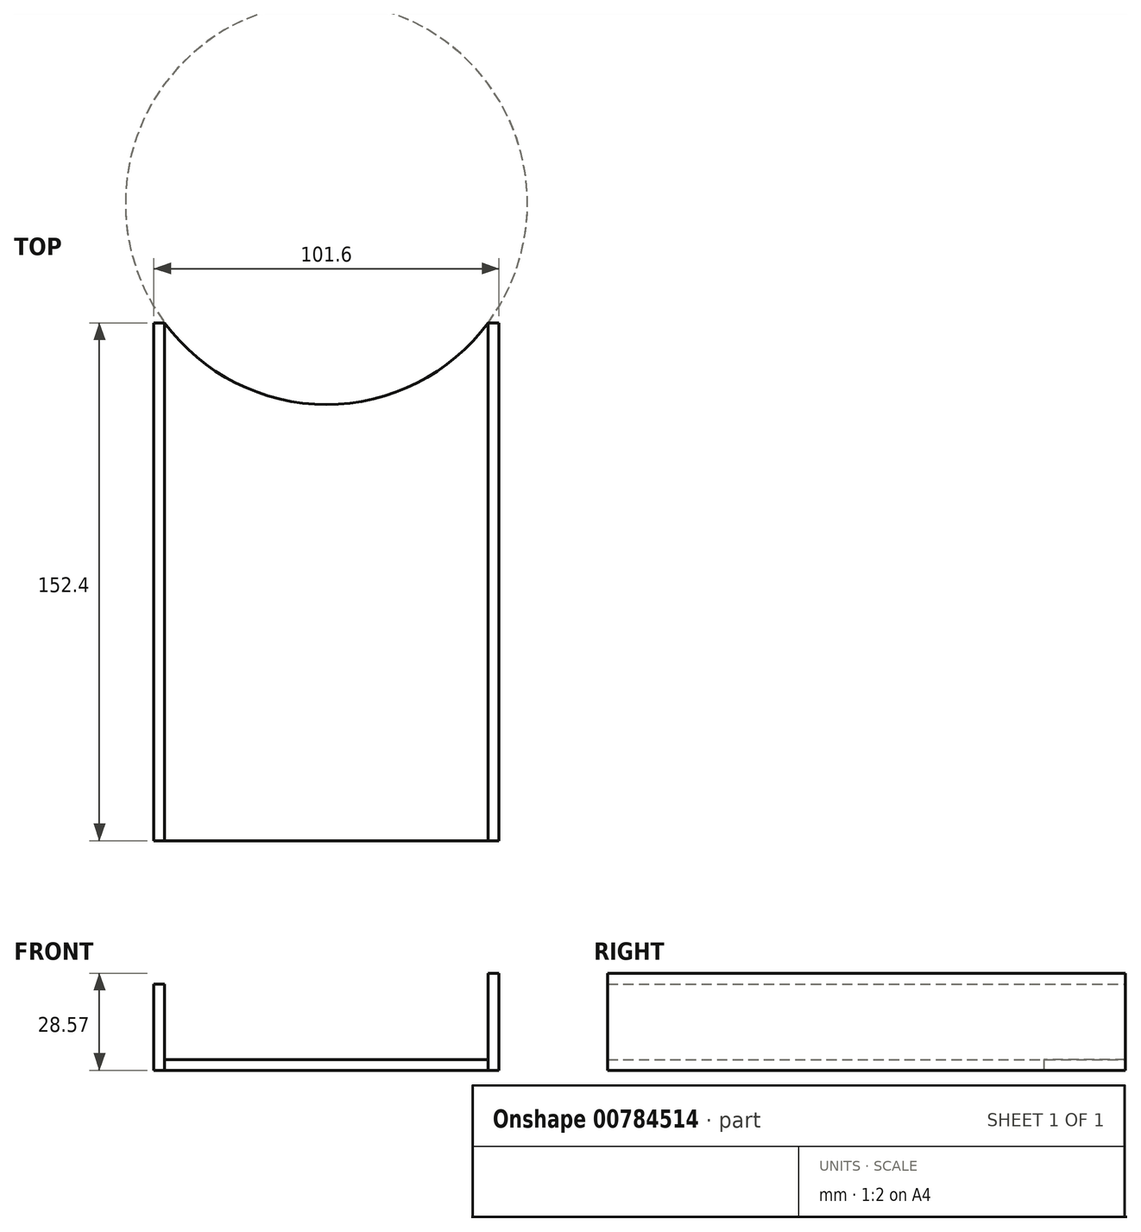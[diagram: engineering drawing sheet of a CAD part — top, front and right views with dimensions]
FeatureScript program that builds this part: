
annotation { "Feature Type Name" : "Feature", "Feature Type Description" : "" }
export const myFeature = defineFeature(function(context is Context, id is Id, definition is map)
    precondition{}
    {
        {
            var Q0;
            Q0=qCreatedBy(makeId("Top.planeOp"),FACE);
            var sketch = newSketch(context, id + "F0", { "sketchPlane" : qUnion([Q0])});
            skPoint(sketch, "E0.MirrorCS.end.orphan", {"position": v(0, -9.2) * mm});
            skLineSegment(sketch, "E1", {"start": v(-43.7, -71.47) * mm, "end": v(57.9, -71.47) * mm});
            skArc(sketch, "E2", {"start": v(-40.52, 80.93) * mm, "mid": v(7.1, 56.89) * mm, "end": v(54.73, 80.93) * mm});
            skLineSegment(sketch, "E3", {"start": v(-43.7, -71.47) * mm, "end": v(-40.52, -71.47) * mm});
            skLineSegment(sketch, "E4", {"start": v(-40.52, -71.47) * mm, "end": v(-40.52, 80.93) * mm});
            skLineSegment(sketch, "E5", {"start": v(57.9, -71.47) * mm, "end": v(54.73, -71.47) * mm});
            skLineSegment(sketch, "E6", {"start": v(54.73, -71.47) * mm, "end": v(54.73, 80.93) * mm});
            skLineSegment(sketch, "E7", {"start": v(-40.52, -71.47) * mm, "end": v(54.73, -71.47) * mm});
            skLineSegment(sketch, "E8", {"start": v(-40.52, -68.3) * mm, "end": v(-40.52, -71.47) * mm});
            skLineSegment(sketch, "E9", {"start": v(54.73, -63.53) * mm, "end": v(54.73, -71.47) * mm});
            skLineSegment(sketch, "E10", {"start": v(54.73, 80.93) * mm, "end": v(61.42, 80.93) * mm});
            skLineSegment(sketch, "E11", {"start": v(61.42, 80.93) * mm, "end": v(61.42, -71.47) * mm});
            skLineSegment(sketch, "E12", {"start": v(61.42, -71.47) * mm, "end": v(54.73, -71.47) * mm});
            skSolve(sketch);
        }
        {
            var Q0;
            {var subQ0=sQuery(id+"F0.wireOp",EDGE,"E2");Q0=makeQuery(id+"F0.imprint","IMPRINT",FACE,{"disambiguationData":[TD([[makeQuery(id+"F0.imprint","IMPRINT",EDGE,{"derivedFrom":subQ0}),-1.0]])]});}
            extrude(context, id + "F1", {"entities" : qUnion([Q0]), "depth" : 3.17 * mm, "offsetDistance" : 25.4 * mm});
        }
        {
            var Q0;
            Q0=qCreatedBy(makeId("Top.planeOp"),FACE);
            var sketch = newSketch(context, id + "F2", { "sketchPlane" : qUnion([Q0])});
            skLineSegment(sketch, "E13", {"start": v(54.73, 80.93) * mm, "end": v(54.73, -71.47) * mm});
            skLineSegment(sketch, "E14", {"start": v(54.73, -71.47) * mm, "end": v(57.9, -71.47) * mm});
            skLineSegment(sketch, "E15", {"start": v(57.9, -71.47) * mm, "end": v(57.9, 80.93) * mm});
            skLineSegment(sketch, "E16", {"start": v(57.9, 80.93) * mm, "end": v(54.73, 80.93) * mm});
            skLineSegment(sketch, "E17", {"start": v(-40.52, 80.93) * mm, "end": v(-43.7, 80.93) * mm});
            skLineSegment(sketch, "E18", {"start": v(-43.7, 80.93) * mm, "end": v(-43.7, -71.47) * mm});
            skLineSegment(sketch, "E19", {"start": v(-43.7, -71.47) * mm, "end": v(-40.52, -71.47) * mm});
            skLineSegment(sketch, "E20", {"start": v(-40.52, -71.47) * mm, "end": v(-40.52, 80.93) * mm});
            skSolve(sketch);
        }
        {
            var Q0;
            Q0=makeQuery(id+"F2.imprint","IMPRINT",FACE,{"disambiguationData":[TD([[makeQuery(id+"F2.imprint","IMPRINT",EDGE,{"derivedFrom":sQuery(id+"F2.wireOp",EDGE,"E13")}),1.0]])]});
            extrude(context, id + "F3", {"entities" : qUnion([Q0]), "depth" : 28.57 * mm, "offsetDistance" : 25.4 * mm});
        }
        {
            var Q0;
            Q0=makeQuery(id+"F2.imprint","IMPRINT",FACE,{"disambiguationData":[TD([[makeQuery(id+"F2.imprint","IMPRINT",EDGE,{"derivedFrom":sQuery(id+"F2.wireOp",EDGE,"E17")}),1.0]])]});
            extrude(context, id + "F4", {"entities" : qUnion([Q0]), "depth" : 25.4 * mm, "offsetDistance" : 25.4 * mm});
        }
    });
